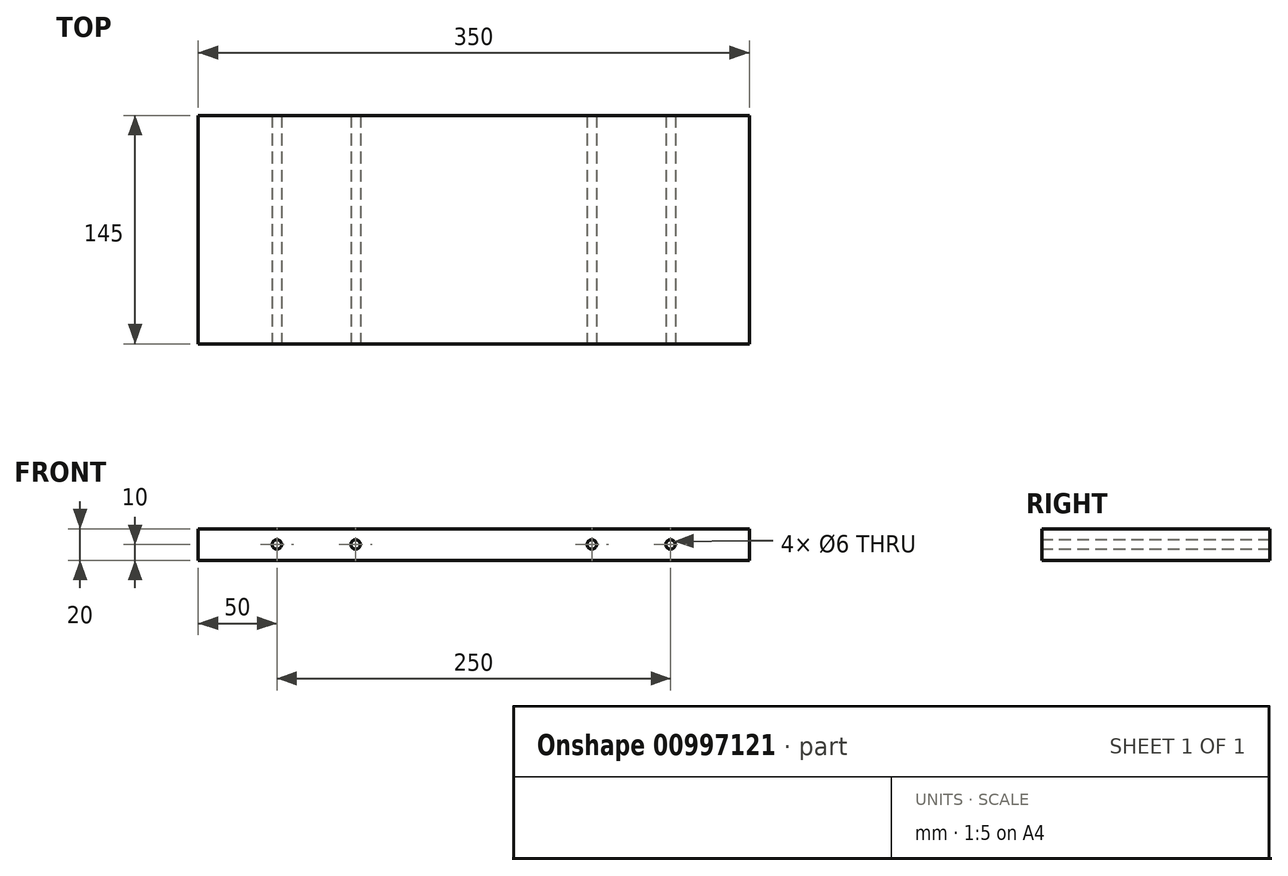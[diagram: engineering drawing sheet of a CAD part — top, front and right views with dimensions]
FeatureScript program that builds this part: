
annotation { "Feature Type Name" : "Feature", "Feature Type Description" : "" }
export const myFeature = defineFeature(function(context is Context, id is Id, definition is map)
    precondition{}
    {
        {
            var Q0;
            Q0=qCreatedBy(makeId("Top.planeOp"),FACE);
            var sketch = newSketch(context, id + "F0", { "sketchPlane" : qUnion([Q0])});
            skLineSegment(sketch, "E0.bottom", {"start": v(175, 72.5) * mm, "end": v(-175, 72.5) * mm});
            skLineSegment(sketch, "E0.top", {"start": v(175, -72.5) * mm, "end": v(-175, -72.5) * mm});
            skLineSegment(sketch, "E0.left", {"start": v(175, 72.5) * mm, "end": v(175, -72.5) * mm});
            skLineSegment(sketch, "E0.right", {"start": v(-175, 72.5) * mm, "end": v(-175, -72.5) * mm});
            skPoint(sketch, "E0.middle", {"position": v(0, 0) * mm});
            skSolve(sketch);
        }
        {
            var Q0;
            Q0=qSketchRegion(id+"F0",true);
            extrude(context, id + "F1", {"entities" : qUnion([Q0]), "endBound" : BoundingType.SYMMETRIC, "depth" : 20 * mm, "offsetDistance" : 25 * mm});
        }
        {
            var Q0;
            Q0=makeQuery(id+"F1.opExtrude","SWEPT_FACE",FACE,{"disambiguationData":[OSD([sQuery(id+"F0.wireOp",EDGE,"E0.top")])]});
            var sketch = newSketch(context, id + "F2", { "sketchPlane" : qUnion([Q0])});
            skPoint(sketch, "E1", {"position": v(-125, 0) * mm});
            skPoint(sketch, "E2", {"position": v(-75, 0) * mm});
            skPoint(sketch, "E3", {"position": v(75, 0) * mm});
            skPoint(sketch, "E4", {"position": v(125, 0) * mm});
            skSolve(sketch);
        }
        {
            var Q0;
            Q0=sQuery(id+"F2.wireOp",VERTEX,"E1");
            var Q1;
            Q1=sQuery(id+"F2.wireOp",VERTEX,"E2");
            var Q2;
            Q2=sQuery(id+"F2.wireOp",VERTEX,"E3");
            var Q3;
            Q3=sQuery(id+"F2.wireOp",VERTEX,"E4");
            var Q4;
            Q4=makeQuery(id+"F1.opExtrude","SWEPT_BODY",BODY,{"disambiguationData":[OSD([sQuery(id+"F0.wireOp",EDGE,"E0.bottom"),sQuery(id+"F0.wireOp",EDGE,"E0.top"),sQuery(id+"F0.wireOp",EDGE,"E0.left"),sQuery(id+"F0.wireOp",EDGE,"E0.right")])]});
            hole(context, id + "F3", {"style" : HoleStyle.SIMPLE, "endStyle" : HoleEndStyle.THROUGH, "holeDiameter" : 6 * mm, "majorDiameter" : 5 * mm, "isTappedThrough" : true, "tappedDepth" : 12 * mm, "tapClearance" : 3, "locations" : qUnion([Q0, Q1, Q2, Q3]), "scope" : qUnion([Q4])});
        }
    });
